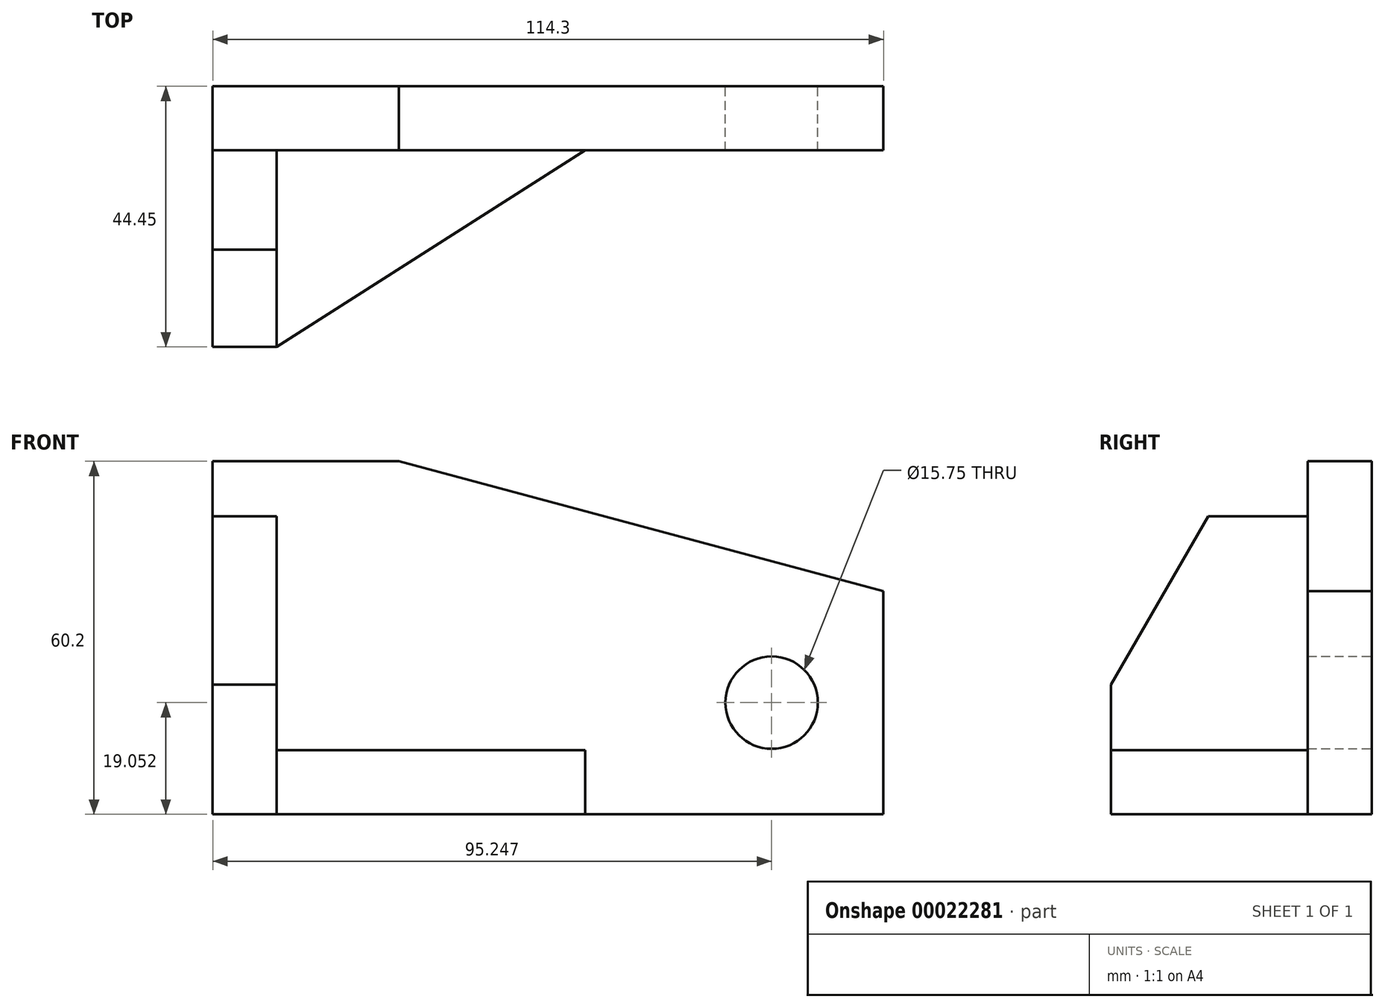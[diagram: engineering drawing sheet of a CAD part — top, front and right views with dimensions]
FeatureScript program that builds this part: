
annotation { "Feature Type Name" : "Feature", "Feature Type Description" : "" }
export const myFeature = defineFeature(function(context is Context, id is Id, definition is map)
    precondition{}
    {
        {
            var Q0;
            Q0=qCreatedBy(makeId("Front.planeOp"),FACE);
            var sketch = newSketch(context, id + "F0", { "sketchPlane" : qUnion([Q0])});
            skLineSegment(sketch, "E0.bottom", {"start": v(-58.52, 42.94) * mm, "end": v(-26.77, 42.94) * mm});
            skLineSegment(sketch, "E0.top", {"start": v(-58.52, -17.26) * mm, "end": v(55.78, -17.26) * mm});
            skLineSegment(sketch, "E0.left", {"start": v(-58.52, 42.94) * mm, "end": v(-58.52, -17.26) * mm});
            skLineSegment(sketch, "E0.right", {"start": v(55.78, 20.82) * mm, "end": v(55.78, -17.26) * mm});
            skLineSegment(sketch, "E1", {"start": v(-26.77, 42.94) * mm, "end": v(55.78, 20.82) * mm});
            skCircle(sketch, "E2", {"center": v(36.73, 1.8) * mm, "radius": 7.87 * mm});
            skSolve(sketch);
        }
        {
            var Q0;
            Q0 = qSketchRegion(id + "F0Hnfrf0JIgqGLe_0", true);
            var Q1;
            Q1 = qSketchRegion(id + "F0", true);
            extrude(context, id + "F1", {"entities" : qUnion([Q0, Q1]), "depth" : 10.92 * mm});
        }
        {
            var Q0;
            Q0=makeQuery(id+"F1.opExtrude","CAP_FACE",FACE,{"disambiguationData":[OSD([sQuery(id+"F0.wireOp",EDGE,"E0.bottom"),sQuery(id+"F0.wireOp",EDGE,"E0.top"),sQuery(id+"F0.wireOp",EDGE,"E0.left"),sQuery(id+"F0.wireOp",EDGE,"E0.right"),sQuery(id+"F0.wireOp",EDGE,"E1"),sQuery(id+"F0.wireOp",EDGE,"E2")])],"isStart":false});
            var sketch = newSketch(context, id + "F2", { "sketchPlane" : qUnion([Q0])});
            skLineSegment(sketch, "E3.bottom", {"start": v(-58.52, -6.34) * mm, "end": v(4.98, -6.34) * mm});
            skLineSegment(sketch, "E3.top", {"start": v(-58.52, -17.26) * mm, "end": v(4.98, -17.26) * mm});
            skLineSegment(sketch, "E3.left", {"start": v(-58.52, -6.34) * mm, "end": v(-58.52, -17.26) * mm});
            skLineSegment(sketch, "E3.right", {"start": v(4.98, -6.34) * mm, "end": v(4.98, -17.26) * mm});
            skSolve(sketch);
        }
        {
            var Q0;
            Q0=makeQuery(id+"F2.imprint","IMPRINT",FACE,{"disambiguationData":[TD([[makeQuery(id+"F2.imprint","IMPRINT",EDGE,{"derivedFrom":sQuery(id+"F2.wireOp",EDGE,"E3.bottom")}),-1.0]])]});
            extrude(context, id + "F3", {"entities" : qUnion([Q0]), "operationType" : NewBodyOperationType.ADD, "depth" : 33.53 * mm});
        }
        {
            var Q0;
            Q0=makeQuery(id+"F3.opExtrude","SWEPT_FACE",FACE,{"disambiguationData":[OSD([sQuery(id+"F2.wireOp",EDGE,"E3.bottom")])]});
            var sketch = newSketch(context, id + "F4", { "sketchPlane" : qUnion([Q0])});
            skLineSegment(sketch, "E4", {"start": v(-47.6, -44.45) * mm, "end": v(4.98, -10.92) * mm});
            skSolve(sketch);
        }
        {
            var Q0;
            {var subQ2=sQuery(id+"F4.wireOp",EDGE,"E4");Q0=makeQuery(id+"F4.imprint","IMPRINT",FACE,{"disambiguationData":[TD([[makeQuery(id+"F4.imprint","IMPRINT",EDGE,{"derivedFrom":subQ2}),-1.0]])]});}
            extrude(context, id + "F5", {"entities" : qUnion([Q0]), "operationType" : NewBodyOperationType.REMOVE, "oppositeDirection" : true, "depth" : 25.4 * mm});
        }
        {
            var Q0;
            Q0=makeQuery(id+"F1.opExtrude","CAP_FACE",FACE,{"disambiguationData":[OSD([sQuery(id+"F0.wireOp",EDGE,"E0.bottom"),sQuery(id+"F0.wireOp",EDGE,"E0.top"),sQuery(id+"F0.wireOp",EDGE,"E0.left"),sQuery(id+"F0.wireOp",EDGE,"E0.right"),sQuery(id+"F0.wireOp",EDGE,"E1"),sQuery(id+"F0.wireOp",EDGE,"E2")])],"isStart":false});
            var sketch = newSketch(context, id + "F6", { "sketchPlane" : qUnion([Q0])});
            skLineSegment(sketch, "E5.bottom", {"start": v(-58.52, 42.94) * mm, "end": v(-47.6, 42.94) * mm});
            skLineSegment(sketch, "E5.top", {"start": v(-58.52, -6.34) * mm, "end": v(-47.6, -6.34) * mm});
            skLineSegment(sketch, "E5.left", {"start": v(-58.52, 42.94) * mm, "end": v(-58.52, -6.34) * mm});
            skLineSegment(sketch, "E5.right", {"start": v(-47.6, 42.94) * mm, "end": v(-47.6, -6.34) * mm});
            skSolve(sketch);
        }
        {
            var Q0;
            Q0=makeQuery(id+"F6.imprint","IMPRINT",FACE,{"disambiguationData":[TD([[makeQuery(id+"F6.imprint","IMPRINT",EDGE,{"derivedFrom":sQuery(id+"F6.wireOp",EDGE,"E5.bottom")}),-1.0]])]});
            extrude(context, id + "F7", {"entities" : qUnion([Q0]), "operationType" : NewBodyOperationType.ADD, "depth" : 33.53 * mm});
        }
        {
            var Q0;
            Q0=makeQuery(id+"F7.boolean.opBoolean","MERGE",FACE,{"derivedFrom":[makeQuery(id+"F3.boolean.opBoolean","MERGE",FACE,{"derivedFrom":[makeQuery(id+"F1.opExtrude","SWEPT_FACE",FACE,{"disambiguationData":[OSD([sQuery(id+"F0.wireOp",EDGE,"E0.left")])]}),makeQuery(id+"F3.opExtrude","SWEPT_FACE",FACE,{"disambiguationData":[OSD([sQuery(id+"F2.wireOp",EDGE,"E3.left")])]})]}),makeQuery(id+"F7.opExtrude","SWEPT_FACE",FACE,{"disambiguationData":[OSD([sQuery(id+"F6.wireOp",EDGE,"E5.left")])]})]});
            var sketch = newSketch(context, id + "F8", { "sketchPlane" : qUnion([Q0])});
            skLineSegment(sketch, "E6", {"start": v(44.45, 4.84) * mm, "end": v(22.45, 42.94) * mm});
            skSolve(sketch);
        }
        {
            var Q0;
            {var subQ2=sQuery(id+"F8.wireOp",EDGE,"E6");Q0=makeQuery(id+"F8.imprint","IMPRINT",FACE,{"disambiguationData":[TD([[makeQuery(id+"F8.imprint","IMPRINT",EDGE,{"derivedFrom":subQ2}),-1.0]])]});}
            extrude(context, id + "F9", {"entities" : qUnion([Q0]), "operationType" : NewBodyOperationType.REMOVE, "oppositeDirection" : true, "depth" : 25.4 * mm});
        }
        {
            var Q0;
            Q0=makeQuery(id+"F7.boolean.opBoolean","MERGE",FACE,{"derivedFrom":[makeQuery(id+"F3.boolean.opBoolean","MERGE",FACE,{"derivedFrom":[makeQuery(id+"F1.opExtrude","SWEPT_FACE",FACE,{"disambiguationData":[OSD([sQuery(id+"F0.wireOp",EDGE,"E0.left")])]}),makeQuery(id+"F3.opExtrude","SWEPT_FACE",FACE,{"disambiguationData":[OSD([sQuery(id+"F2.wireOp",EDGE,"E3.left")])]})]}),makeQuery(id+"F7.opExtrude","SWEPT_FACE",FACE,{"disambiguationData":[OSD([sQuery(id+"F6.wireOp",EDGE,"E5.left")])]})]});
            var sketch = newSketch(context, id + "F10", { "sketchPlane" : qUnion([Q0])});
            skLineSegment(sketch, "E7.bottom", {"start": v(10.92, 42.94) * mm, "end": v(42.56, 42.94) * mm});
            skLineSegment(sketch, "E7.top", {"start": v(10.92, 33.54) * mm, "end": v(42.56, 33.54) * mm});
            skLineSegment(sketch, "E7.left", {"start": v(10.92, 42.94) * mm, "end": v(10.92, 33.54) * mm});
            skLineSegment(sketch, "E7.right", {"start": v(42.56, 42.94) * mm, "end": v(42.56, 33.54) * mm});
            skSolve(sketch);
        }
        {
            var Q0;
            {var subQ5=sQuery(id+"F10.wireOp",EDGE,"E7.left");Q0=makeQuery(id+"F10.imprint","IMPRINT",FACE,{"disambiguationData":[TD([[makeQuery(id+"F10.imprint","IMPRINT",EDGE,{"derivedFrom":subQ5}),1.0]])]});}
            extrude(context, id + "F11", {"entities" : qUnion([Q0]), "operationType" : NewBodyOperationType.REMOVE, "oppositeDirection" : true, "depth" : 25.4 * mm});
        }
    });
